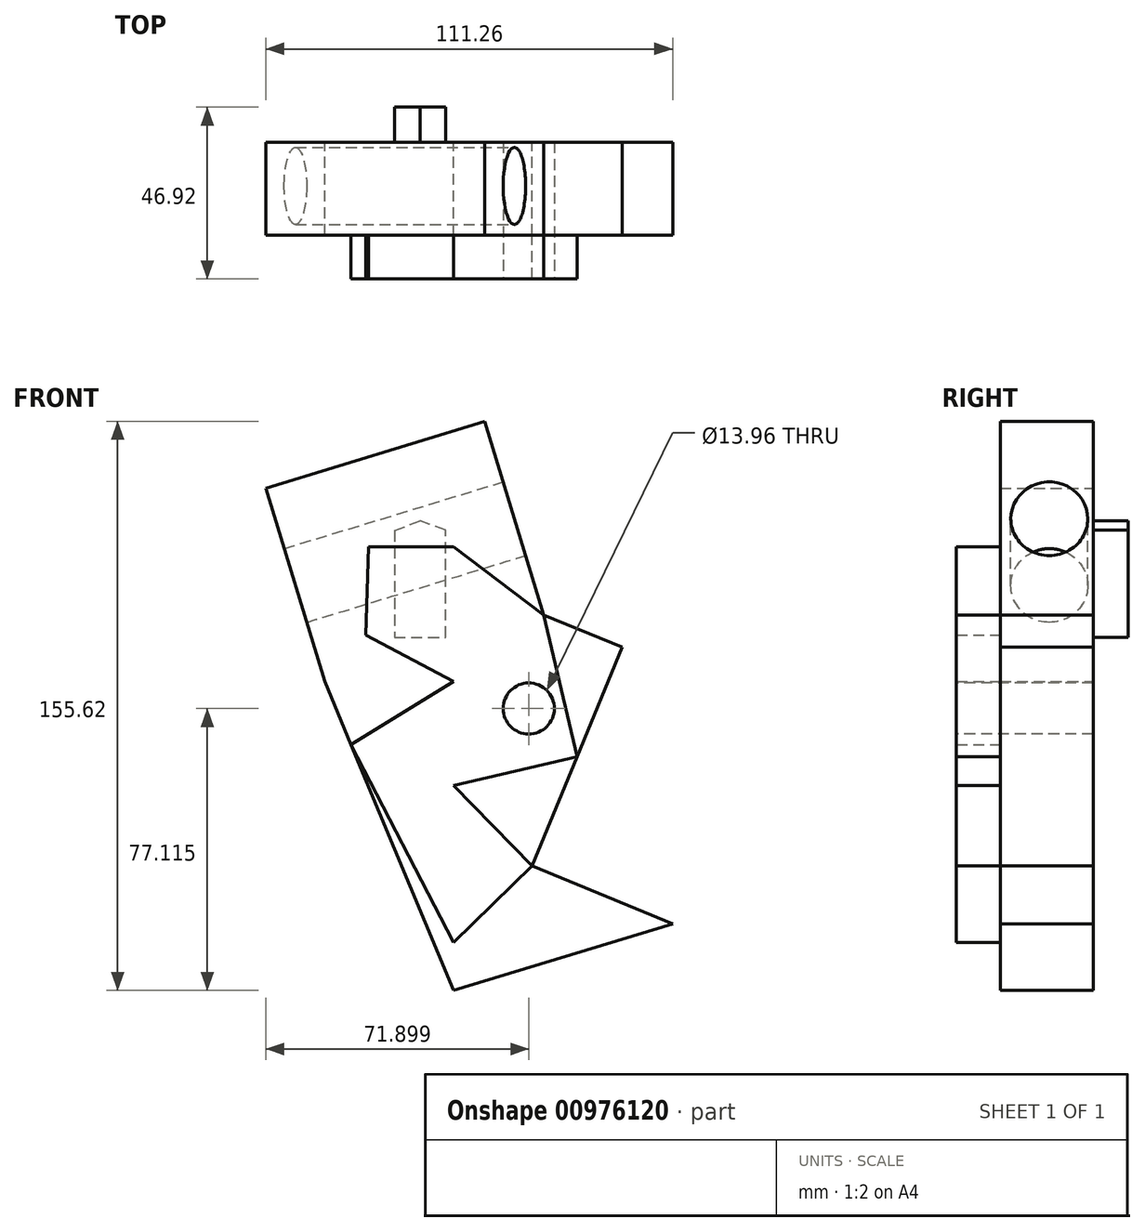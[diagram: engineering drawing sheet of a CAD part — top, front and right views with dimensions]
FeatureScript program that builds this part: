
annotation { "Feature Type Name" : "Feature", "Feature Type Description" : "" }
export const myFeature = defineFeature(function(context is Context, id is Id, definition is map)
    precondition{}
    {
        {
            var Q0;
            Q0=qCreatedBy(makeId("Front.planeOp"),FACE);
            var sketch = newSketch(context, id + "F0", { "sketchPlane" : qUnion([Q0])});
            skLineSegment(sketch, "E0", {"start": v(-35.26, 0) * mm, "end": v(24.6, 18.25) * mm});
            skLineSegment(sketch, "E1", {"start": v(24.6, 18.25) * mm, "end": v(0, -41.61) * mm});
            skLineSegment(sketch, "E2", {"start": v(0, -41.61) * mm, "end": v(59.86, -66.2) * mm});
            skLineSegment(sketch, "E3", {"start": v(59.86, -66.2) * mm, "end": v(0, -84.46) * mm});
            skLineSegment(sketch, "E4", {"start": v(0, -84.46) * mm, "end": v(-35.26, 0) * mm});
            skSolve(sketch);
        }
        {
            var Q0;
            Q0 = qSketchRegion(id + "F0", true);
            extrude(context, id + "F1", {"entities" : qUnion([Q0]), "depth" : 25.4 * mm, "offsetDistance" : 25.4 * mm});
        }
        {
            var Q0;
            Q0=makeQuery(id+"F1.opExtrude","SWEPT_FACE",FACE,{"disambiguationData":[OSD([sQuery(id+"F0.wireOp",EDGE,"E1")])]});
            extrude(context, id + "F2", {"entities" : qUnion([Q0]), "operationType" : NewBodyOperationType.ADD, "depth" : 23.16 * mm, "offsetDistance" : 25.4 * mm});
        }
        {
            var Q0;
            Q0=makeQuery(id+"F1.opExtrude","SWEPT_FACE",FACE,{"disambiguationData":[OSD([sQuery(id+"F0.wireOp",EDGE,"E0")])]});
            extrude(context, id + "F3", {"entities" : qUnion([Q0]), "operationType" : NewBodyOperationType.ADD, "depth" : 55.32 * mm, "offsetDistance" : 25.4 * mm});
        }
        {
            var Q0;
            Q0=makeQuery(id+"F3.opExtrude","SWEPT_FACE",FACE,{"disambiguationData":[OSD([sQuery(id+"F0.wireOp",EDGE,"E0"),sQuery(id+"F0.wireOp",EDGE,"E1")])]});
            var sketch = newSketch(context, id + "F4", { "sketchPlane" : qUnion([Q0])});
            skCircle(sketch, "E5", {"center": v(-11.96, 37.78) * mm, "radius": 10.53 * mm});
            skSolve(sketch);
        }
        {
            var Q0;
            Q0 = qSketchRegion(id + "F4", true);
            extrude(context, id + "F5", {"entities" : qUnion([Q0]), "operationType" : NewBodyOperationType.REMOVE, "oppositeDirection" : true, "depth" : 108.9 * mm, "offsetDistance" : 25.4 * mm});
        }
        {
            var Q0;
            {var subQ0=sQuery(id+"F0.wireOp",EDGE,"E0");var subQ1=sQuery(id+"F0.wireOp",EDGE,"E1");Q0=makeQuery(id+"F3.boolean.opBoolean","MERGE",FACE,{"derivedFrom":[makeQuery(id+"F2.boolean.opBoolean","MERGE",FACE,{"derivedFrom":[makeQuery(id+"F1.opExtrude","CAP_FACE",FACE,{"disambiguationData":[OSD([subQ0,subQ1,sQuery(id+"F0.wireOp",EDGE,"E2"),sQuery(id+"F0.wireOp",EDGE,"E3"),sQuery(id+"F0.wireOp",EDGE,"E4")])],"isStart":false}),makeQuery(id+"F2.opExtrude","SWEPT_FACE",FACE,{"disambiguationData":[OSD([subQ1]),TDD([makeQuery(id+"F1.opExtrude","CAP_EDGE",EDGE,{"disambiguationData":[OSD([subQ1])],"isStart":false})])]})]}),makeQuery(id+"F3.opExtrude","SWEPT_FACE",FACE,{"disambiguationData":[OSD([subQ0]),TDD([makeQuery(id+"F1.opExtrude","CAP_EDGE",EDGE,{"disambiguationData":[OSD([subQ0])],"isStart":false})])]})]});}
            var sketch = newSketch(context, id + "F6", { "sketchPlane" : qUnion([Q0])});
            skLineSegment(sketch, "E6", {"start": v(-23.7, 36.9) * mm, "end": v(0, 36.9) * mm});
            skLineSegment(sketch, "E7", {"start": v(0, 36.9) * mm, "end": v(24.6, 18.25) * mm});
            skLineSegment(sketch, "E8", {"start": v(24.6, 18.25) * mm, "end": v(33.72, -20.48) * mm});
            skLineSegment(sketch, "E9", {"start": v(33.72, -20.48) * mm, "end": v(0, -28.42) * mm});
            skLineSegment(sketch, "E10", {"start": v(0, -28.42) * mm, "end": v(21.42, -50.41) * mm});
            skLineSegment(sketch, "E11", {"start": v(21.42, -50.41) * mm, "end": v(0, -71.28) * mm});
            skLineSegment(sketch, "E12", {"start": v(0, -71.28) * mm, "end": v(-28.09, -17.19) * mm});
            skLineSegment(sketch, "E13", {"start": v(-28.09, -17.19) * mm, "end": v(0, 0) * mm});
            skLineSegment(sketch, "E14", {"start": v(0, 0) * mm, "end": v(-24.09, 12.8) * mm});
            skLineSegment(sketch, "E15", {"start": v(-24.09, 12.8) * mm, "end": v(-23.33, 36.9) * mm});
            skSolve(sketch);
        }
        {
            var Q0;
            {var subQ0=sQuery(id+"F6.wireOp",EDGE,"E7");Q0=makeQuery(id+"F6.imprint","IMPRINT",FACE,{"disambiguationData":[TD([[makeQuery(id+"F6.imprint","IMPRINT",EDGE,{"derivedFrom":subQ0}),-1.0]])]});}
            extrude(context, id + "F7", {"entities" : qUnion([Q0]), "operationType" : NewBodyOperationType.ADD, "depth" : 11.94 * mm, "offsetDistance" : 25.4 * mm});
        }
        {
            var Q0;
            Q0=makeQuery(id+"F7.opExtrude","CAP_FACE",FACE,{"disambiguationData":[OSD([sQuery(id+"F6.wireOp",EDGE,"E6"),sQuery(id+"F6.wireOp",EDGE,"E7"),sQuery(id+"F6.wireOp",EDGE,"E8"),sQuery(id+"F6.wireOp",EDGE,"E9"),sQuery(id+"F6.wireOp",EDGE,"E10"),sQuery(id+"F6.wireOp",EDGE,"E11"),sQuery(id+"F6.wireOp",EDGE,"E12"),sQuery(id+"F6.wireOp",EDGE,"E13"),sQuery(id+"F6.wireOp",EDGE,"E14"),sQuery(id+"F6.wireOp",EDGE,"E15")])],"isStart":false});
            var sketch = newSketch(context, id + "F8", { "sketchPlane" : qUnion([Q0])});
            skCircle(sketch, "E16", {"center": v(20.5, -7.35) * mm, "radius": 6.98 * mm});
            skSolve(sketch);
        }
        {
            var Q0;
            Q0=makeQuery(id+"F8.imprint","IMPRINT",FACE,{"disambiguationData":[TD([[makeQuery(id+"F8.imprint","IMPRINT",EDGE,{"derivedFrom":sQuery(id+"F8.wireOp",EDGE,"E16")}),1.0]])]});
            extrude(context, id + "F9", {"entities" : qUnion([Q0]), "operationType" : NewBodyOperationType.REMOVE, "oppositeDirection" : true, "depth" : 59.27 * mm, "offsetDistance" : 25.4 * mm});
        }
        {
            var Q0;
            {var subQ0=sQuery(id+"F0.wireOp",EDGE,"E0");var subQ1=sQuery(id+"F0.wireOp",EDGE,"E1");Q0=makeQuery(id+"F3.boolean.opBoolean","MERGE",FACE,{"derivedFrom":[makeQuery(id+"F2.boolean.opBoolean","MERGE",FACE,{"derivedFrom":[makeQuery(id+"F1.opExtrude","CAP_FACE",FACE,{"disambiguationData":[OSD([subQ0,subQ1,sQuery(id+"F0.wireOp",EDGE,"E2"),sQuery(id+"F0.wireOp",EDGE,"E3"),sQuery(id+"F0.wireOp",EDGE,"E4")])],"isStart":true}),makeQuery(id+"F2.opExtrude","SWEPT_FACE",FACE,{"disambiguationData":[OSD([subQ1]),TDD([makeQuery(id+"F1.opExtrude","CAP_EDGE",EDGE,{"disambiguationData":[OSD([subQ1])],"isStart":true})])]})]}),makeQuery(id+"F3.opExtrude","SWEPT_FACE",FACE,{"disambiguationData":[OSD([subQ0]),TDD([makeQuery(id+"F1.opExtrude","CAP_EDGE",EDGE,{"disambiguationData":[OSD([subQ0])],"isStart":true})])]})]});}
            var sketch = newSketch(context, id + "F10", { "sketchPlane" : qUnion([Q0])});
            skLineSegment(sketch, "E17", {"start": v(16.24, 41.3) * mm, "end": v(9.23, 44.02) * mm});
            skLineSegment(sketch, "E18", {"start": v(16.24, 41.3) * mm, "end": v(16.24, 12.15) * mm});
            skLineSegment(sketch, "E19", {"start": v(16.24, 12.15) * mm, "end": v(2.17, 12.15) * mm});
            skLineSegment(sketch, "E20", {"start": v(2.17, 12.15) * mm, "end": v(2.17, 41.42) * mm});
            skLineSegment(sketch, "E21", {"start": v(2.17, 41.42) * mm, "end": v(9.23, 44.02) * mm});
            skSolve(sketch);
        }
        {
            var Q0;
            Q0 = qSketchRegion(id + "F10", true);
            extrude(context, id + "F11", {"entities" : qUnion([Q0]), "operationType" : NewBodyOperationType.ADD, "depth" : 9.58 * mm, "offsetDistance" : 25.4 * mm});
        }
    });
